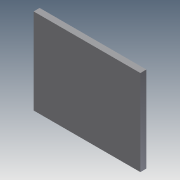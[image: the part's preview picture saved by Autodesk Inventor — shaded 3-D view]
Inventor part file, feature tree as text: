
AUTODESK INVENTOR PART (.ipt)
format: ipt  version: 2011 (Build 150239000, 239)  size: 66,048 bytes
history: native  units: in
note: dims shown in document units (in); Inventor stores cm internally (conversion verified against a paired STEP export)
features: extrude x1, sketch x1
ambient origin geometry x8: Origin, YZ Plane, XZ Plane, XY Plane, X Axis, Y Axis, Z Axis, Center Point
bodies: Solid1 (feature_tree)
feature tree (2):
  extrude  "Extrusion1"  Depth=1.7717in
  sketch  "Sketch1"  dims[d0=2.2047in d1=1.7717in d2=0.125in d3=0.0in]
